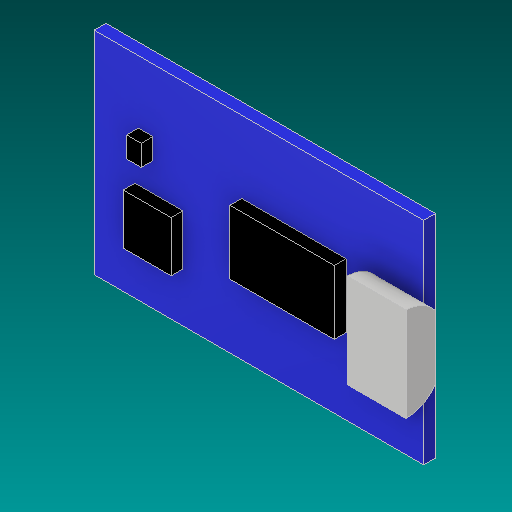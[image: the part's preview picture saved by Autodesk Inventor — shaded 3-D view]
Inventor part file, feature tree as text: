
AUTODESK INVENTOR PART (.ipt)
format: ipt  version: 2019 (Build 230136000, 136)  size: 153,600 bytes
history: native  units: mm
features: extrude x4, sketch x4, projected_geometry x1
ambient origin geometry x8: Origin, YZ Plane, XZ Plane, XY Plane, X Axis, Y Axis, Z Axis, Center Point
bodies: Solid1 (feature_tree)
feature tree (9):
  extrude  "Extrusion1"  Depth=18.0mm
  extrude  "Extrusion2"  Depth=1.0mm TaperAngle=0.0deg
  extrude  "Extrusion3"  Depth=2.5mm
  extrude  "Extrusion4"  Depth=4.0mm
  sketch  "Sketch1"  dims[d0=28.0mm d1=18.0mm]
  sketch  "Sketch2"  dims[d2=28.0mm d3=1.0mm d4=0.0mm]
  sketch  "Sketch3"  dims[d5=1.0mm d6=0.0mm d7=2.5mm]
  sketch  "Sketch4"  dims[d8=4.0mm d9=8.0mm d10=1.0mm d11=0.0mm d12=4.0mm d13=0.0mm]
  projected_geometry  "Projected Loop1"
